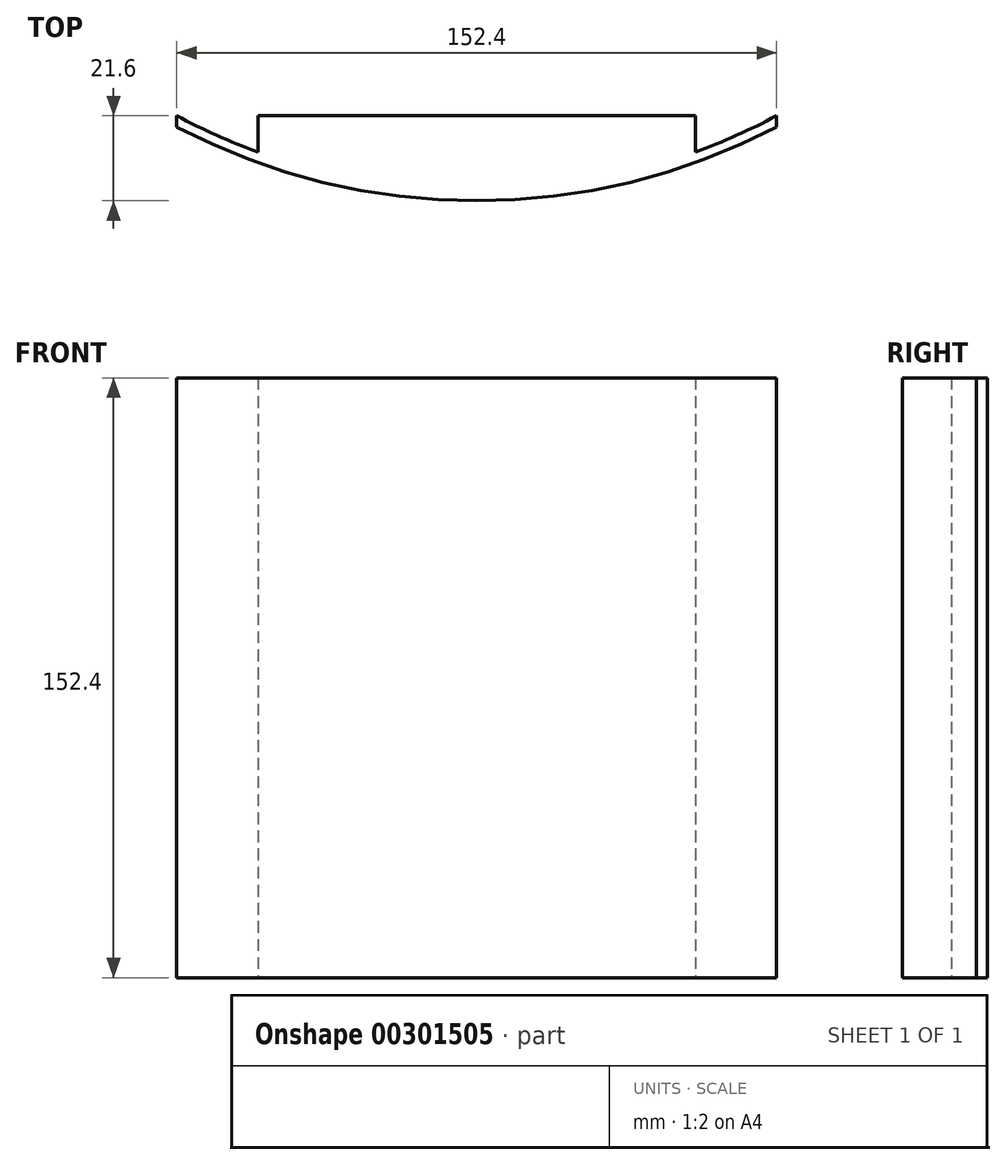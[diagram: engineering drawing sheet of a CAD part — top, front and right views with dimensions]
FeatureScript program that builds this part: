
annotation { "Feature Type Name" : "Feature", "Feature Type Description" : "" }
export const myFeature = defineFeature(function(context is Context, id is Id, definition is map)
    precondition{}
    {
        {
            var Q0;
            Q0=qCreatedBy(makeId("Top.planeOp"),FACE);
            var sketch = newSketch(context, id + "F0", { "sketchPlane" : qUnion([Q0])});
            skLineSegment(sketch, "E0.bottom", {"start": v(55.56, -9.22) * mm, "end": v(-55.56, -9.22) * mm});
            skLineSegment(sketch, "E0.top", {"start": v(55.56, 0) * mm, "end": v(-55.56, 0) * mm});
            skLineSegment(sketch, "E0.left", {"start": v(55.56, -9.22) * mm, "end": v(55.56, 0) * mm});
            skLineSegment(sketch, "E0.right", {"start": v(-55.56, -9.22) * mm, "end": v(-55.56, 0) * mm});
            skArc(sketch, "E1", {"start": v(-76.2, 0) * mm, "mid": v(0, -19.06) * mm, "end": v(76.2, 0) * mm});
            skArc(sketch, "E2", {"start": v(-76.2, -2.87) * mm, "mid": v(0, -21.6) * mm, "end": v(76.2, -2.87) * mm});
            skLineSegment(sketch, "E3", {"start": v(-76.2, -2.87) * mm, "end": v(-76.2, 0) * mm});
            skLineSegment(sketch, "E4", {"start": v(76.2, -2.87) * mm, "end": v(76.2, 0) * mm});
            skSolve(sketch);
        }
        {
            var Q0;
            Q0 = qSketchRegion(id + "F0", true);
            extrude(context, id + "F1", {"entities" : qUnion([Q0]), "depth" : 152.4 * mm});
        }
    });
